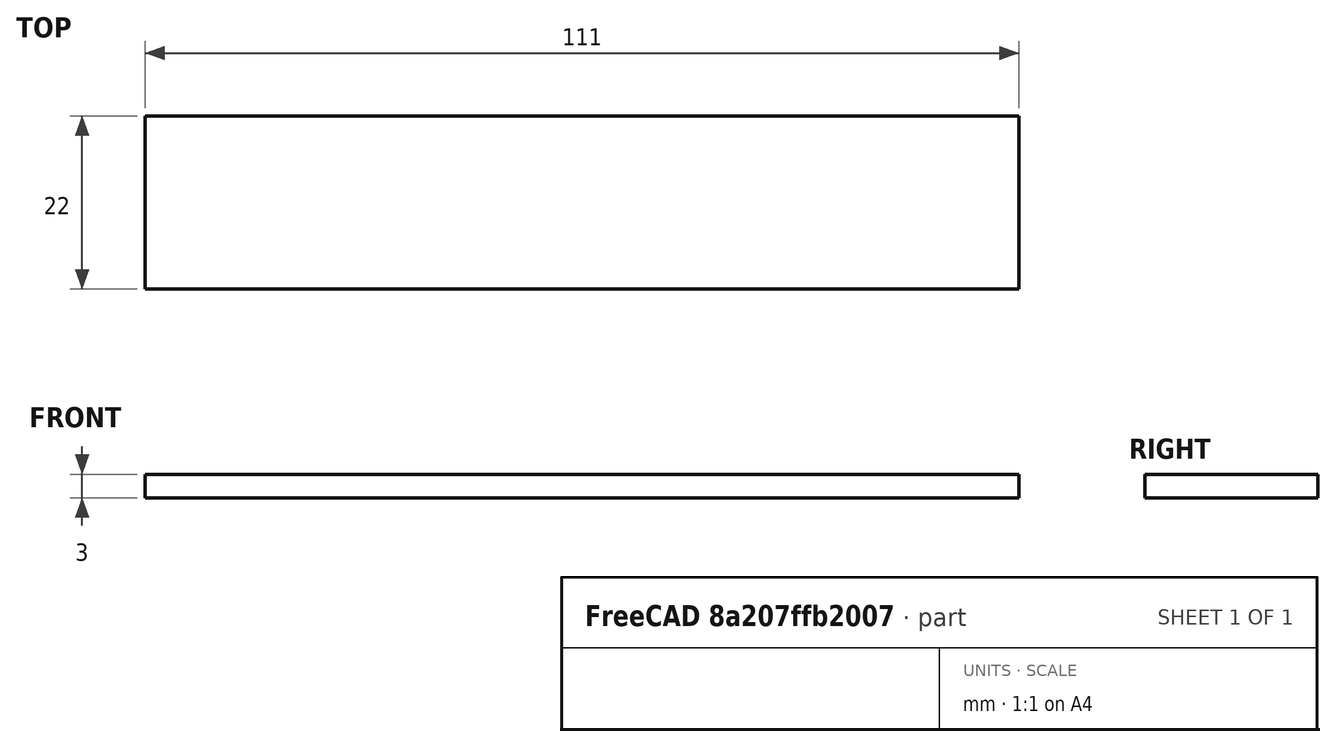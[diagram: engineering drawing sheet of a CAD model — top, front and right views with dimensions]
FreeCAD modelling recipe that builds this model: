
FCSTD DOCUMENT  (FreeCAD 0.17R13541 (Git))
Label: Acry-Base-6-good-sketched-alt
License: All rights reserved
LicenseURL: http://en.wikipedia.org/wiki/All_rights_reserved
objects: Sketcher::SketchObject×2, PartDesign::Pad×1, PartDesign::Body×1, App::Part×1
note: 5 computed .brp shape members not serialized (recipe doc carries the construction recipe); baked Part::Feature solids carry a one-line shape summary decoded from their .brp

FEATURE [Sketcher::SketchObject] Sketch
  MapMode = 5
  Support = -> [XY_Plane001]
  sketch-geometry (6):
    g0: LineSegment StartX=-55.5 StartY=11 StartZ=0 EndX=55.5 EndY=11 EndZ=0
    g1: LineSegment StartX=55.5 StartY=11 StartZ=0 EndX=55.5 EndY=-11 EndZ=0
    g2: LineSegment StartX=55.5 StartY=-11 StartZ=0 EndX=-55.5 EndY=-11 EndZ=0
    g3: LineSegment StartX=-55.5 StartY=-11 StartZ=0 EndX=-55.5 EndY=11 EndZ=0
    g4: GeomPoint X=0 Y=11 Z=0
    g5: GeomPoint X=-55.5 Y=0 Z=0
  constraints (16):
    c: Coincident(g0,g1)
    c: Coincident(g1,g2)
    c: Coincident(g2,g3)
    c: Coincident(g3,g0)
    c: Horizontal(g0)
    c: Horizontal(g2)
    c: Vertical(g1)
    c: Vertical(g3)
    c: Distance(g0) = 111
    c: Distance(g1) = 22
    c: PointOnObject(g4,g0)
    c: PointOnObject(g5,g3)
    c: Symmetric(g0,g2,g5)
    c: Symmetric(g0,g0,g4)
    c: PointOnObject(g4,g-2)
    c: PointOnObject(g5,g-1)
FEATURE [PartDesign::Pad] Pad
  Length = 3
  Length2 = 100
  Profile = -> Sketch
  Type = 0
FEATURE [Sketcher::SketchObject] Sketch001
  ExternalGeometry = -> [Pad]
  MapMode = 5
  Placement = pos=(0,0,3) rot=(0,0,1;0rad)
  Support = -> [Pad]
  sketch-geometry (18):
    g0: LineSegment StartX=-55.5 StartY=11 StartZ=0 EndX=55.5 EndY=11 EndZ=0
    g1: LineSegment StartX=55.5 StartY=11 StartZ=0 EndX=55.5 EndY=4 EndZ=0
    g2: LineSegment StartX=-55.5 StartY=4 StartZ=0 EndX=-55.5 EndY=11 EndZ=0
    g3: LineSegment StartX=-55.5 StartY=-11 StartZ=0 EndX=55.5 EndY=-11 EndZ=0
    g4: LineSegment StartX=55.5 StartY=-11 StartZ=0 EndX=55.5 EndY=-4 EndZ=0
    g5: LineSegment StartX=-55.5 StartY=-4 StartZ=0 EndX=-55.5 EndY=-11 EndZ=0
    g6: LineSegment StartX=-55.5 StartY=-4 StartZ=0 EndX=-50 EndY=-4 EndZ=0
    g7: LineSegment StartX=-50 StartY=-4 StartZ=0 EndX=-50 EndY=-5 EndZ=0
    g8: LineSegment StartX=-50 StartY=-5 StartZ=0 EndX=50 EndY=-5 EndZ=0
    g9: LineSegment StartX=50 StartY=-5 StartZ=0 EndX=50 EndY=-4 EndZ=0
    g10: LineSegment StartX=50 StartY=-4 StartZ=0 EndX=55.5 EndY=-4 EndZ=0
    g11: GeomPoint X=0 Y=-5 Z=0
    g12: LineSegment StartX=55.5 StartY=4 StartZ=0 EndX=50 EndY=4 EndZ=0
    g13: LineSegment StartX=50 StartY=4 StartZ=0 EndX=50 EndY=5 EndZ=0
    g14: LineSegment StartX=50 StartY=5 StartZ=0 EndX=-50 EndY=5 EndZ=0
    g15: LineSegment StartX=-50 StartY=5 StartZ=0 EndX=-50 EndY=4 EndZ=0
    g16: LineSegment StartX=-50 StartY=4 StartZ=0 EndX=-55.5 EndY=4 EndZ=0
    g17: GeomPoint X=0 Y=5 Z=0
  constraints (50):
    c: Coincident(g0,g1)
    c: Coincident(g2,g0)
    c: Horizontal(g0)
    c: Vertical(g1)
    c: Vertical(g2)
    c: Coincident(g0,g-4)
    c: PointOnObject(g1,g-6)
    c: Coincident(g3,g4)
    c: Coincident(g5,g3)
    c: Horizontal(g3)
    c: Vertical(g4)
    c: Vertical(g5)
    c: Coincident(g3,g-5)
    c: PointOnObject(g4,g-6)
    c: Distance(g2,g-1) = 4
    c: Distance(g5,g-1) = 4
    c: Coincident(g5,g6)
    c: Horizontal(g6)
    c: Coincident(g6,g7)
    c: Vertical(g7)
    c: Coincident(g7,g8)
    c: Horizontal(g8)
    c: Coincident(g8,g9)
    c: Vertical(g9)
    c: Coincident(g9,g10)
    c: Coincident(g10,g4)
    c: Horizontal(g10)
    c: Distance(g4,g-1) = 4
    c: Distance(g8,g-1) = 5
    c: Distance(g8) = 100
    c: PointOnObject(g11,g8)
    c: Symmetric(g7,g8,g11)
    c: PointOnObject(g11,g-2)
    c: Coincident(g1,g12)
    c: Horizontal(g12)
    c: Coincident(g12,g13)
    c: Coincident(g13,g14)
    c: Horizontal(g14)
    c: Coincident(g14,g15)
    c: Vertical(g15)
    c: Coincident(g15,g16)
    c: Coincident(g16,g2)
    c: Horizontal(g16)
    c: PointOnObject(g17,g14)
    c: PointOnObject(g17,g-2)
    c: Distance(g14) = 100
    c: Vertical(g13)
    c: Symmetric(g13,g14,g17)
    c: Distance(g17,g-1) = 5
    c: Distance(g1,g-1) = 4
FEATURE [PartDesign::Body] Body
  Group = -> [Sketch,Pad,Sketch001]
  Origin = -> Origin001
  Tip = -> Pad
FEATURE [App::Part] Part
  Group = -> [Body]
  License = CC BY 3.0
  LicenseURL = http://creativecommons.org/licenses/by/3.0/
  Origin = -> Origin
